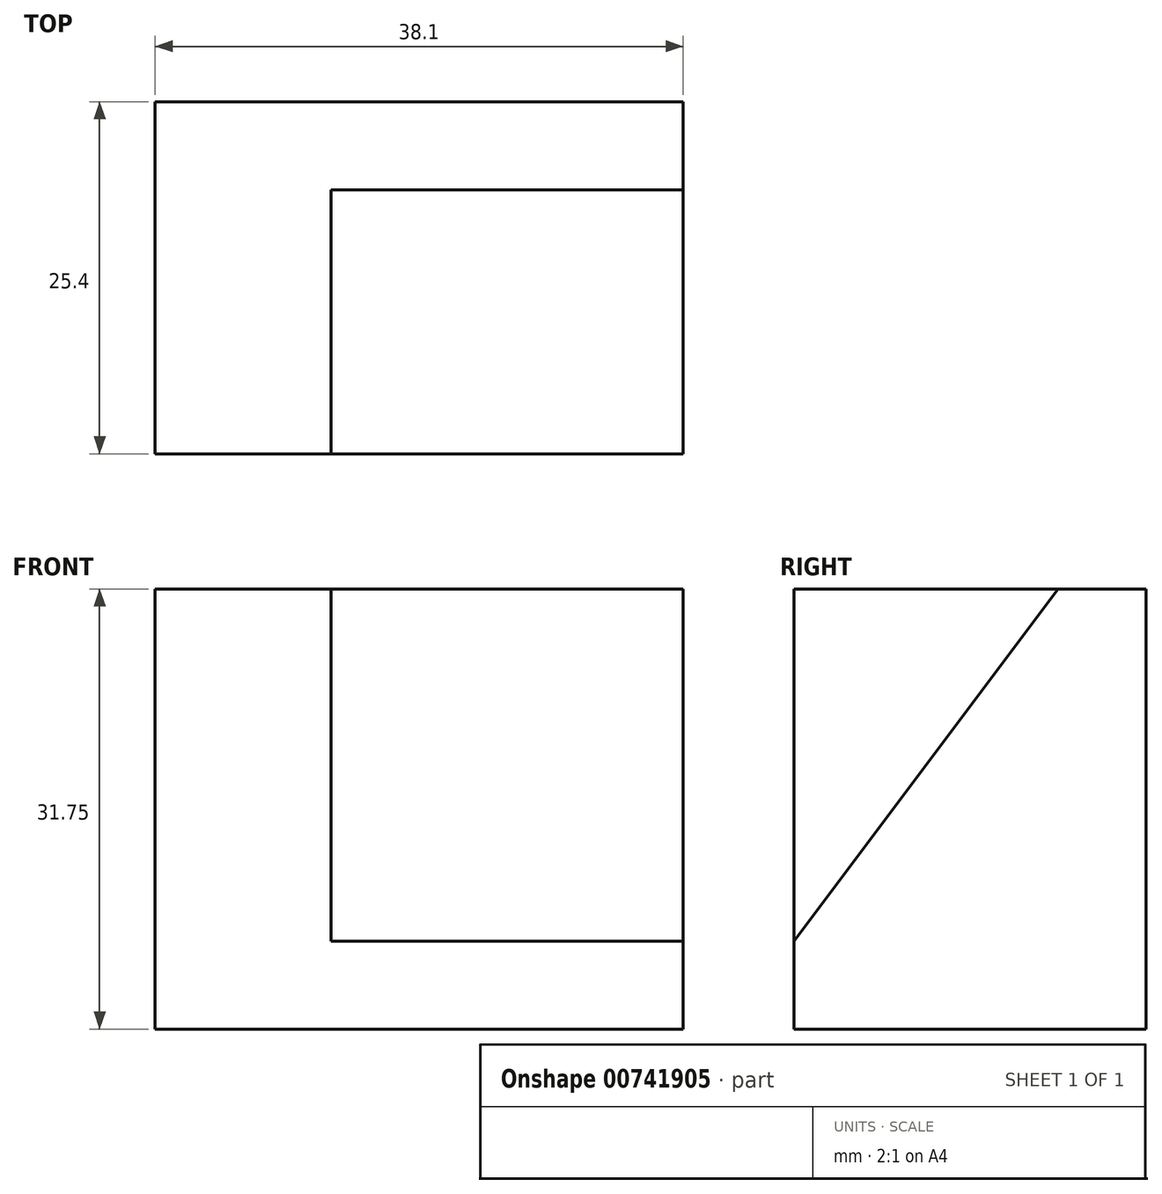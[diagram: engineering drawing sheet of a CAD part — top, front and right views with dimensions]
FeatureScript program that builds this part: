
annotation { "Feature Type Name" : "Feature", "Feature Type Description" : "" }
export const myFeature = defineFeature(function(context is Context, id is Id, definition is map)
    precondition{}
    {
        {
            var Q0;
            Q0=qCreatedBy(makeId("Front.planeOp"),FACE);
            var sketch = newSketch(context, id + "F0", { "sketchPlane" : qUnion([Q0])});
            skLineSegment(sketch, "E0", {"start": v(0, 0) * mm, "end": v(0, 31.75) * mm});
            skLineSegment(sketch, "E1", {"start": v(0, 31.75) * mm, "end": v(38.1, 31.75) * mm});
            skLineSegment(sketch, "E2", {"start": v(38.1, 31.75) * mm, "end": v(38.1, 0) * mm});
            skLineSegment(sketch, "E3", {"start": v(39.34, -0.16) * mm, "end": v(0, 0) * mm});
            skLineSegment(sketch, "E4", {"start": v(0, 0) * mm, "end": v(38.1, 0) * mm});
            skSolve(sketch);
        }
        {
            var Q0;
            Q0=makeQuery(id+"F0.imprint","IMPRINT",FACE,{"disambiguationData":[TD([[makeQuery(id+"F0.imprint","IMPRINT",EDGE,{"derivedFrom":sQuery(id+"F0.wireOp",EDGE,"E0")}),-1.0]])]});
            extrude(context, id + "F1", {"entities" : qUnion([Q0]), "depth" : 25.4 * mm, "offsetDistance" : 25.4 * mm});
        }
        {
            var Q0;
            Q0=makeQuery(id+"F1.opExtrude","SWEPT_FACE",FACE,{"disambiguationData":[OSD([sQuery(id+"F0.wireOp",EDGE,"E2")])]});
            var sketch = newSketch(context, id + "F2", { "sketchPlane" : qUnion([Q0])});
            skLineSegment(sketch, "E5", {"start": v(0, 31.75) * mm, "end": v(-6.35, 31.75) * mm});
            skLineSegment(sketch, "E6", {"start": v(-6.35, 31.75) * mm, "end": v(-25.4, 6.35) * mm});
            skLineSegment(sketch, "E7", {"start": v(-25.4, 6.35) * mm, "end": v(-25.4, 0) * mm});
            skSolve(sketch);
        }
        {
            var Q0;
            {var subQ0=sQuery(id+"F2.wireOp",EDGE,"E6");Q0=makeQuery(id+"F2.imprint","IMPRINT",FACE,{"disambiguationData":[TD([[makeQuery(id+"F2.imprint","IMPRINT",EDGE,{"derivedFrom":subQ0}),-1.0]])]});}
            extrude(context, id + "F3", {"entities" : qUnion([Q0]), "operationType" : NewBodyOperationType.REMOVE, "oppositeDirection" : true, "depth" : 25.4 * mm, "offsetDistance" : 25.4 * mm});
        }
    });
